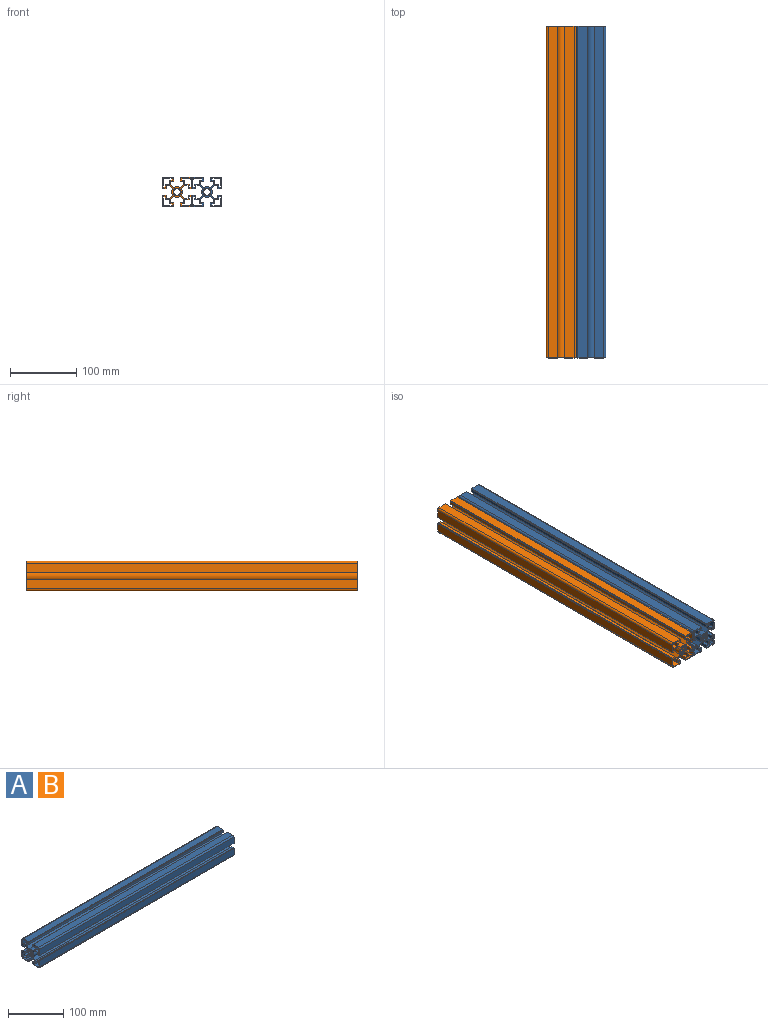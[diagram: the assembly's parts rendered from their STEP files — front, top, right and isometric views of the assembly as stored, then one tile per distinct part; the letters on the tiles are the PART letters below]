
ASSEMBLY  parts=2 mates=1
PART A: 134 faces, bbox 500x45x45 mm
  f0: cylinder r=5mm len=500mm, axis (1,0,0), area 872.7mm2, adj f4,f111,f112,f133
  f1: cylinder r=8mm len=500mm, axis (1,0,0), area 5129.2mm2, adj f4,f58,f101,f133
  f2: plane 500x13.7mm, normal (0,1,0), area 6850mm2, adj f3,f4,f5,f133
  f3: cylinder r=3mm len=500mm, axis (1,0,0), area 2356.2mm2, adj f2,f4,f6,f133
  f4: plane 45x45mm, normal (-1,0,0), area 560mm2, adj f0,f1,f2,f3,f5,f6,f7,f8
  f5: plane 500x1.5mm, normal (0,0,-1), area 750mm2, adj f2,f4,f102,f133
  f6: plane 500x13.7mm, normal (0,0,1), area 6850mm2, adj f3,f4,f103,f133
  f7: cylinder r=6.1mm len=500mm, axis (1,0,0), area 1330.8mm2, adj f4,f104,f105,f133
  f8: cylinder r=5mm len=500mm, axis (1,0,0), area 872.7mm2, adj f4,f105,f106,f133
  f9: cylinder r=6.1mm len=500mm, axis (1,0,0), area 1330.8mm2, adj f4,f106,f107,f133
  f10: cylinder r=5mm len=500mm, axis (1,0,0), area 872.7mm2, adj f4,f107,f108,f133
  f11: cylinder r=6.1mm len=500mm, axis (1,0,0), area 1330.8mm2, adj f4,f108,f109,f133
  f12: cylinder r=5mm len=500mm, axis (1,0,0), area 872.7mm2, adj f4,f109,f110,f133
  f13: cylinder r=6.1mm len=500mm, axis (1,0,0), area 1330.8mm2, adj f4,f110,f111,f133
  f14: cylinder r=6.1mm len=500mm, axis (1,0,0), area 1330.8mm2, adj f4,f112,f113,f133
  f15: cylinder r=5mm len=500mm, axis (1,0,0), area 872.7mm2, adj f4,f113,f114,f133
  f16: cylinder r=6.1mm len=500mm, axis (1,0,0), area 1330.8mm2, adj f4,f114,f115,f133
  f17: cylinder r=5mm len=500mm, axis (1,0,0), area 872.7mm2, adj f4,f115,f116,f133
  f18: cylinder r=6.1mm len=500mm, axis (1,0,0), area 1330.8mm2, adj f4,f116,f117,f133
  f19: cylinder r=5mm len=500mm, axis (1,0,0), area 872.7mm2, adj f4,f117,f118,f133
  f20: cylinder r=6.1mm len=500mm, axis (1,0,0), area 1330.8mm2, adj f4,f118,f119,f133
  f21: cylinder r=5mm len=500mm, axis (1,0,0), area 872.7mm2, adj f4,f104,f119,f133
  f22: cylinder r=2.5mm len=500mm, axis (1,0,0), area 1963.5mm2, adj f4,f23,f30,f133
  f23: plane 500x11mm, normal (0,-1,0), area 5500mm2, adj f4,f22,f24,f133
  f24: plane 500x3mm, normal (0,0,1), area 1500mm2, adj f4,f23,f25,f133
  f25: plane 500x4.05mm, normal (0,1,0), area 2025mm2, adj f4,f24,f26,f133
  f26: plane 500x6.45mm, normal (0,0,1), area 3225mm2, adj f4,f25,f27,f133
  f27: plane 500x6.45mm, normal (0,1,0), area 3225mm2, adj f4,f26,f28,f133
  f28: plane 500x4.05mm, normal (0,0,1), area 2025mm2, adj f4,f27,f29,f133
  f29: plane 500x3mm, normal (0,1,0), area 1500mm2, adj f4,f28,f30,f133
  f30: plane 500x11mm, normal (0,0,-1), area 5500mm2, adj f4,f22,f29,f133
  f31: plane 500x3mm, normal (0,-1,0), area 1500mm2, adj f4,f32,f39,f133
  f32: plane 500x4.05mm, normal (0,0,1), area 2025mm2, adj f4,f31,f33,f133
  f33: plane 500x6.45mm, normal (0,-1,0), area 3225mm2, adj f4,f32,f34,f133
  f34: plane 500x6.45mm, normal (0,0,1), area 3225mm2, adj f4,f33,f35,f133
  f35: plane 500x4.05mm, normal (0,-1,0), area 2025mm2, adj f4,f34,f36,f133
  f36: plane 500x3mm, normal (0,0,1), area 1500mm2, adj f4,f35,f37,f133
  f37: plane 500x11mm, normal (0,1,0), area 5500mm2, adj f4,f36,f38,f133
  f38: cylinder r=2.5mm len=500mm, axis (1,0,0), area 1963.5mm2, adj f4,f37,f39,f133
  f39: plane 500x11mm, normal (0,0,-1), area 5500mm2, adj f4,f31,f38,f133
  f40: plane 500x3mm, normal (0,0,-1), area 1500mm2, adj f4,f41,f48,f133
  f41: plane 500x4.05mm, normal (0,-1,0), area 2025mm2, adj f4,f40,f42,f133
  f42: plane 500x6.45mm, normal (0,0,-1), area 3225mm2, adj f4,f41,f43,f133
  f43: plane 500x6.45mm, normal (0,-1,0), area 3225mm2, adj f4,f42,f44,f133
  f44: plane 500x4.05mm, normal (0,0,-1), area 2025mm2, adj f4,f43,f45,f133
  f45: plane 500x3mm, normal (0,-1,0), area 1500mm2, adj f4,f44,f46,f133
  f46: plane 500x11mm, normal (0,0,1), area 5500mm2, adj f4,f45,f47,f133
  f47: cylinder r=2.5mm len=500mm, axis (1,0,0), area 1963.5mm2, adj f4,f46,f48,f133
  f48: plane 500x11mm, normal (0,1,0), area 5500mm2, adj f4,f40,f47,f133
  f49: cylinder r=2.5mm len=500mm, axis (1,0,0), area 1963.5mm2, adj f4,f50,f57,f133
  f50: plane 500x11mm, normal (0,0,1), area 5500mm2, adj f4,f49,f51,f133
  f51: plane 500x3mm, normal (0,1,0), area 1500mm2, adj f4,f50,f52,f133
  f52: plane 500x4.05mm, normal (0,0,-1), area 2025mm2, adj f4,f51,f53,f133
  f53: plane 500x6.45mm, normal (0,1,0), area 3225mm2, adj f4,f52,f54,f133
  f54: plane 500x6.45mm, normal (0,0,-1), area 3225mm2, adj f4,f53,f55,f133
  f55: plane 500x4.05mm, normal (0,1,0), area 2025mm2, adj f4,f54,f56,f133
  f56: plane 500x3mm, normal (0,0,-1), area 1500mm2, adj f4,f55,f57,f133
  f57: plane 500x11mm, normal (0,-1,0), area 5500mm2, adj f4,f49,f56,f133
  f58: plane 500x5.27mm, normal (0,-0.71,-0.71), area 3723mm2, adj f1,f4,f59,f133
  f59: plane 500x4.82mm, normal (0,-1,0), area 2411.8mm2, adj f4,f58,f60,f133
  f60: plane 500x5.05mm, normal (0,0,1), area 2525mm2, adj f4,f59,f61,f133
  f61: plane 500x4.5mm, normal (0,-1,0), area 2250mm2, adj f4,f60,f120,f133
  f62: plane 500x13.7mm, normal (0,0,-1), area 6850mm2, adj f4,f63,f121,f133
  f63: cylinder r=3mm len=500mm, axis (1,0,0), area 2356.2mm2, adj f4,f62,f64,f133
  f64: plane 500x13.7mm, normal (0,1,0), area 6850mm2, adj f4,f63,f122,f133
  f65: plane 500x4.5mm, normal (0,0,1), area 2250mm2, adj f4,f66,f123,f133
  f66: plane 500x5.05mm, normal (0,-1,0), area 2525mm2, adj f4,f65,f67,f133
  f67: plane 500x4.82mm, normal (0,0,1), area 2411.8mm2, adj f4,f66,f68,f133
  f68: plane 500x5.27mm, normal (0,0.71,0.71), area 3723mm2, adj f4,f67,f69,f133
  f69: cylinder r=8mm len=500mm, axis (1,0,0), area 5129.2mm2, adj f4,f68,f70,f133
  f70: plane 500x5.27mm, normal (0,0.71,-0.71), area 3723mm2, adj f4,f69,f71,f133
  f71: plane 500x4.82mm, normal (0,0,-1), area 2411.8mm2, adj f4,f70,f72,f133
  f72: plane 500x5.05mm, normal (0,-1,0), area 2525mm2, adj f4,f71,f73,f133
  f73: plane 500x4.5mm, normal (0,0,-1), area 2250mm2, adj f4,f72,f102,f133
  f74: plane 500x4.5mm, normal (0,-1,0), area 2250mm2, adj f4,f75,f124,f133
  f75: plane 500x5.05mm, normal (0,0,-1), area 2525mm2, adj f4,f74,f76,f133
  f76: plane 500x4.82mm, normal (0,-1,0), area 2411.8mm2, adj f4,f75,f77,f133
  f77: plane 500x5.27mm, normal (0,-0.71,0.71), area 3723mm2, adj f4,f76,f78,f133
  f78: cylinder r=8mm len=500mm, axis (1,0,0), area 5129.2mm2, adj f4,f77,f79,f133
  f79: plane 500x5.27mm, normal (0,0.71,0.71), area 3723mm2, adj f4,f78,f80,f133
  f80: plane 500x4.82mm, normal (0,1,0), area 2411.8mm2, adj f4,f79,f81,f133
  f81: plane 500x5.05mm, normal (0,0,-1), area 2525mm2, adj f4,f80,f82,f133
  f82: plane 500x4.5mm, normal (0,1,0), area 2250mm2, adj f4,f81,f125,f133
  f83: plane 500x13.7mm, normal (0,0,1), area 6850mm2, adj f4,f84,f126,f133
  f84: cylinder r=3mm len=500mm, axis (1,0,0), area 2356.2mm2, adj f4,f83,f85,f133
  f85: plane 500x13.7mm, normal (0,-1,0), area 6850mm2, adj f4,f84,f127,f133
  f86: plane 500x4.5mm, normal (0,0,-1), area 2250mm2, adj f4,f87,f128,f133
  f87: plane 500x5.05mm, normal (0,1,0), area 2525mm2, adj f4,f86,f88,f133
  f88: plane 500x4.82mm, normal (0,0,-1), area 2411.8mm2, adj f4,f87,f89,f133
  f89: plane 500x5.27mm, normal (0,-0.71,-0.71), area 3723mm2, adj f4,f88,f90,f133
  f90: cylinder r=8mm len=500mm, axis (1,0,0), area 5129.2mm2, adj f4,f89,f91,f133
  f91: plane 500x5.27mm, normal (0,-0.71,0.71), area 3723mm2, adj f4,f90,f92,f133
  f92: plane 500x4.82mm, normal (0,0,1), area 2411.8mm2, adj f4,f91,f93,f133
  f93: plane 500x5.05mm, normal (0,1,0), area 2525mm2, adj f4,f92,f94,f133
  f94: plane 500x4.5mm, normal (0,0,1), area 2250mm2, adj f4,f93,f129,f133
  f95: plane 500x13.7mm, normal (0,-1,0), area 6850mm2, adj f4,f96,f130,f133
  f96: cylinder r=3mm len=500mm, axis (1,0,0), area 2356.2mm2, adj f4,f95,f97,f133
  f97: plane 500x13.7mm, normal (0,0,-1), area 6850mm2, adj f4,f96,f131,f133
  f98: plane 500x4.5mm, normal (0,1,0), area 2250mm2, adj f4,f99,f132,f133
  f99: plane 500x5.05mm, normal (0,0,1), area 2525mm2, adj f4,f98,f100,f133
  f100: plane 500x4.82mm, normal (0,1,0), area 2411.8mm2, adj f4,f99,f101,f133
  f101: plane 500x5.27mm, normal (0,0.71,-0.71), area 3723mm2, adj f1,f4,f100,f133
  f102: plane 500x0.8mm, normal (0,1,0), area 400mm2, adj f4,f5,f73,f133
  f103: plane 500x1.5mm, normal (0,-1,0), area 750mm2, adj f4,f6,f124,f133
  f104: plane 500x1.08mm, normal (0,0.98,-0.17), area 550mm2, adj f4,f7,f21,f133
  f105: plane 500x0.9mm, normal (0,-0.82,0.57), area 550mm2, adj f4,f7,f8,f133
  f106: plane 500x0.9mm, normal (0,0.57,-0.82), area 550mm2, adj f4,f8,f9,f133
  f107: plane 500x1.08mm, normal (0,-0.17,0.98), area 550mm2, adj f4,f9,f10,f133
  f108: plane 500x1.08mm, normal (0,-0.17,-0.98), area 550mm2, adj f4,f10,f11,f133
  f109: plane 500x0.9mm, normal (0,0.57,0.82), area 550mm2, adj f4,f11,f12,f133
  f110: plane 500x0.9mm, normal (0,-0.82,-0.57), area 550mm2, adj f4,f12,f13,f133
  f111: plane 500x1.08mm, normal (0,0.98,0.17), area 550mm2, adj f0,f4,f13,f133
  f112: plane 500x1.08mm, normal (0,-0.98,0.17), area 550mm2, adj f0,f4,f14,f133
  f113: plane 500x0.9mm, normal (0,0.82,-0.57), area 550mm2, adj f4,f14,f15,f133
  f114: plane 500x0.9mm, normal (0,-0.57,0.82), area 550mm2, adj f4,f15,f16,f133
  f115: plane 500x1.08mm, normal (0,0.17,-0.98), area 550mm2, adj f4,f16,f17,f133
  f116: plane 500x1.08mm, normal (0,0.17,0.98), area 550mm2, adj f4,f17,f18,f133
  f117: plane 500x0.9mm, normal (0,-0.57,-0.82), area 550mm2, adj f4,f18,f19,f133
  f118: plane 500x0.9mm, normal (0,0.82,0.57), area 550mm2, adj f4,f19,f20,f133
  f119: plane 500x1.08mm, normal (0,-0.98,-0.17), area 550mm2, adj f4,f20,f21,f133
  f120: plane 500x0.8mm, normal (0,0,-1), area 400mm2, adj f4,f61,f121,f133
  f121: plane 500x1.5mm, normal (0,-1,0), area 750mm2, adj f4,f62,f120,f133
  f122: plane 500x1.5mm, normal (0,0,1), area 750mm2, adj f4,f64,f123,f133
  f123: plane 500x0.8mm, normal (0,1,0), area 400mm2, adj f4,f65,f122,f133
  f124: plane 500x0.8mm, normal (0,0,1), area 400mm2, adj f4,f74,f103,f133
  f125: plane 500x0.8mm, normal (0,0,1), area 400mm2, adj f4,f82,f126,f133
  f126: plane 500x1.5mm, normal (0,1,0), area 750mm2, adj f4,f83,f125,f133
  f127: plane 500x1.5mm, normal (0,0,-1), area 750mm2, adj f4,f85,f128,f133
  f128: plane 500x0.8mm, normal (0,-1,0), area 400mm2, adj f4,f86,f127,f133
  f129: plane 500x0.8mm, normal (0,-1,0), area 400mm2, adj f4,f94,f130,f133
  f130: plane 500x1.5mm, normal (0,0,1), area 750mm2, adj f4,f95,f129,f133
  f131: plane 500x1.5mm, normal (0,1,0), area 750mm2, adj f4,f97,f132,f133
  f132: plane 500x0.8mm, normal (0,0,-1), area 400mm2, adj f4,f98,f131,f133
  f133: plane 45x45mm, normal (1,0,0), area 560mm2, adj f0,f1,f2,f3,f5,f6,f7,f8
PART B: same geometry as A
PLACE A rot(axis=(0,0,1),90deg) t=(132.7,-217.31,72.6)mm
PLACE B rot(axis=(0,0,1),90deg) t=(87.7,-217.31,72.6)mm
MATE fastened A.f133 <-> B.f133  axis (0,1,0) through (110.2,282.69,85.25)mm
